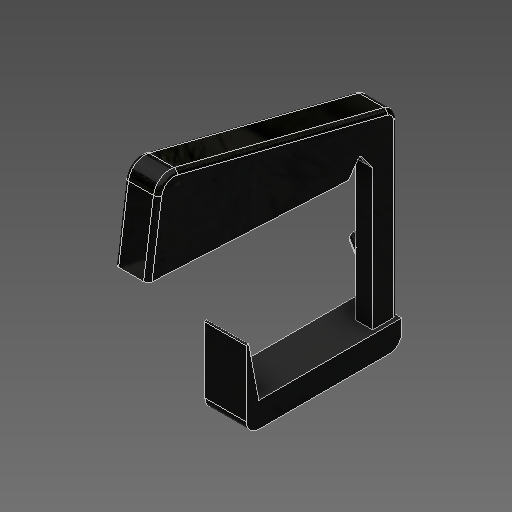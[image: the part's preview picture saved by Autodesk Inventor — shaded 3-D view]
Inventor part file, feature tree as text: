
AUTODESK INVENTOR PART (.ipt)
format: ipt  version: 2020 (Build 240168000, 168)  size: 294,400 bytes
history: native  units: mm
features: extrude x6, fillet x6, other x3, draft x1, chamfer x1
ambient origin geometry x8: Origin, YZ Plane, XZ Plane, XY Plane, X Axis, Y Axis, Z Axis, Center Point
bodies: Solid1 (feature_tree)
feature tree (17):
  extrude  "Key"  Depth=11.0mm
  other  "Hinge Cut Sketch"
  extrude  "Hinge Cut"  TaperAngle=0.0deg  [1 undecoded]
  extrude  "Hinge Cut 2"  Depth=14.835299mm
  other  "Lever Sketch"
  extrude  "Vertical Lever"  Depth=1.0mm
  extrude  "Horizontal Lever"  Depth=10.0mm TaperAngle=0.0deg
  fillet  "Fillet4"  Radius=3.0mm
  fillet  "Fillet5"  Radius=3.0mm
  fillet  "Fillet6"  Radius=33.6625mm
  extrude  "Extrusion12"  Depth=0.5mm
  draft  "FaceDraft3"
  chamfer  "Chamfer1"  Distance=3.0mm
  fillet  "Fillet9"  Radius=6.0mm
  fillet  "Fillet10"  Radius=4.0mm
  fillet  "Fillet11"  Radius=10.0mm
  other  "Key Sketch"
note: 1 required parameter value undecoded (feature->parameter linkage not recoverable at this tier; creation-order binding heuristic only, values carry confidence <= 0.55)
